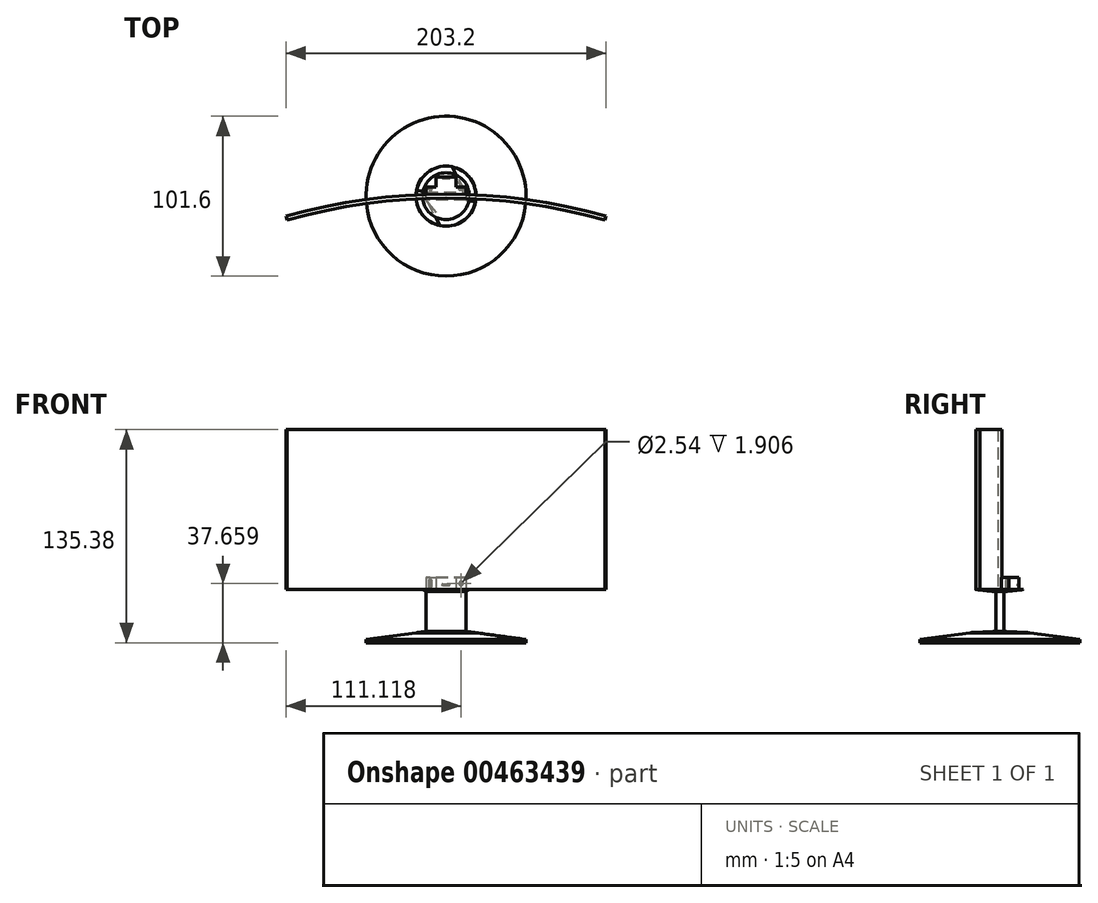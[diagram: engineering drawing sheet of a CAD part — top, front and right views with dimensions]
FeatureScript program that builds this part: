
annotation { "Feature Type Name" : "Feature", "Feature Type Description" : "" }
export const myFeature = defineFeature(function(context is Context, id is Id, definition is map)
    precondition{}
    {
        {
            var Q0;
            Q0=qCreatedBy(makeId("Top.planeOp"),FACE);
            var sketch = newSketch(context, id + "F0", { "sketchPlane" : qUnion([Q0])});
            skCircle(sketch, "E0", {"center": v(0, 0) * mm, "radius": 50.8 * mm});
            skSolve(sketch);
        }
        {
            var Q0;
            Q0=qCreatedBy(makeId("Top.planeOp"),FACE);
            cPlane(context, id + "F1", {"entities" : qUnion([Q0]), "cplaneType" : CPlaneType.OFFSET, "offset" : 4.32 * mm, "width" : 152.4 * mm, "height" : 152.4 * mm});
        }
        {
            var Q0;
            Q0=qCreatedBy(id+"F1.planeOp",FACE);
            var sketch = newSketch(context, id + "F2", { "sketchPlane" : qUnion([Q0])});
            skCircle(sketch, "E1", {"center": v(0, 0) * mm, "radius": 19.05 * mm});
            skSolve(sketch);
        }
        {
            var Q0;
            Q0=makeQuery(id+"F0.imprint","IMPRINT",FACE,{"disambiguationData":[TD([[makeQuery(id+"F0.imprint","IMPRINT",EDGE,{"derivedFrom":sQuery(id+"F0.wireOp",EDGE,"E0")}),1.0]])]});
            var Q1;
            Q1=makeQuery(id+"F2.imprint","IMPRINT",FACE,{"disambiguationData":[TD([[makeQuery(id+"F2.imprint","IMPRINT",EDGE,{"derivedFrom":sQuery(id+"F2.wireOp",EDGE,"E1")}),1.0]])]});
            loft(context, id + "F3", {"sheetProfilesArray" : [{ "sheetProfileEntities" : qUnion([Q0]) }, { "sheetProfileEntities" : qUnion([Q1]) }]});
        }
        {
            var Q0;
            Q0=qCreatedBy(makeId("Top.planeOp"),FACE);
            var sketch = newSketch(context, id + "F4", { "sketchPlane" : qUnion([Q0])});
            skCircle(sketch, "E2", {"center": v(0, 0) * mm, "radius": 50.8 * mm});
            skSolve(sketch);
        }
        {
            var Q0;
            Q0 = qSketchRegion(id + "F4", true);
            extrude(context, id + "F5", {"entities" : qUnion([Q0]), "operationType" : NewBodyOperationType.ADD, "depth" : -2.03 * mm});
        }
        {
            var Q0;
            Q0=qCreatedBy(makeId("Top.planeOp"),FACE);
            cPlane(context, id + "F6", {"entities" : qUnion([Q0]), "cplaneType" : CPlaneType.OFFSET, "offset" : 5.08 * mm, "width" : 152.4 * mm, "height" : 152.4 * mm});
        }
        {
            var Q0;
            Q0=qCreatedBy(id+"F6.planeOp",FACE);
            var sketch = newSketch(context, id + "F7", { "sketchPlane" : qUnion([Q0])});
            skLineSegment(sketch, "E3", {"start": v(-12.7, 2.54) * mm, "end": v(12.7, 2.54) * mm});
            skLineSegment(sketch, "E4", {"start": v(12.7, 2.54) * mm, "end": v(12.7, -2.54) * mm});
            skLineSegment(sketch, "E5", {"start": v(12.7, -2.54) * mm, "end": v(-12.7, -2.54) * mm});
            skPoint(sketch, "E6.end.orphan", {"position": v(-12.7, 0) * mm});
            skLineSegment(sketch, "E7", {"start": v(-12.7, -2.54) * mm, "end": v(-12.7, 2.54) * mm});
            skSolve(sketch);
        }
        {
            var Q0;
            Q0=makeQuery(id+"F7.imprint","IMPRINT",FACE,{"disambiguationData":[TD([[makeQuery(id+"F7.imprint","IMPRINT",EDGE,{"derivedFrom":sQuery(id+"F7.wireOp",EDGE,"E3")}),-1.0]])]});
            var Q1;
            Q1=makeQuery(id+"F3.opLoft","CAP_FACE",FACE,{"disambiguationData":[OSD([makeQuery(id+"F2.imprint","IMPRINT",FACE,{"disambiguationData":[TD([[makeQuery(id+"F2.imprint","IMPRINT",EDGE,{"derivedFrom":sQuery(id+"F2.wireOp",EDGE,"E1")}),1.0]])]})])],"isStart":true});
            loft(context, id + "F8", {"sheetProfilesArray" : [{ "sheetProfileEntities" : qUnion([Q0]) }, { "sheetProfileEntities" : qUnion([Q1]) }]});
        }
        {
            var Q0;
            Q0 = qSketchRegion(id + "F7", true);
            extrude(context, id + "F9", {"entities" : qUnion([Q0]), "operationType" : NewBodyOperationType.ADD, "depth" : 25.4 * mm});
        }
        {
            var Q0;
            Q0=qCreatedBy(makeId("Top.planeOp"),FACE);
            cPlane(context, id + "F10", {"entities" : qUnion([Q0]), "cplaneType" : CPlaneType.OFFSET, "offset" : 31.75 * mm, "width" : 152.4 * mm, "height" : 152.4 * mm});
        }
        {
            var Q0;
            Q0=qCreatedBy(id+"F10.planeOp",FACE);
            var sketch = newSketch(context, id + "F11", { "sketchPlane" : qUnion([Q0])});
            skCircle(sketch, "E8", {"center": v(0, 0) * mm, "radius": 14.86 * mm});
            skSolve(sketch);
        }
        {
            var Q1;
            Q1=makeQuery(id+"F9.opExtrude","CAP_FACE",FACE,{"disambiguationData":[OSD([sQuery(id+"F7.wireOp",EDGE,"E3"),sQuery(id+"F7.wireOp",EDGE,"E4"),sQuery(id+"F7.wireOp",EDGE,"E5"),sQuery(id+"F7.wireOp",EDGE,"E7")])],"isStart":false});
            var Q2;
            Q2=makeQuery(id+"F11.imprint","IMPRINT",FACE,{"disambiguationData":[TD([[makeQuery(id+"F11.imprint","IMPRINT",EDGE,{"derivedFrom":sQuery(id+"F11.wireOp",EDGE,"E8")}),1.0]])]});
            loft(context, id + "F12", {"operationType" : NewBodyOperationType.ADD, "sheetProfilesArray" : [{ "sheetProfileEntities" : qUnion([Q1]) }, { "sheetProfileEntities" : qUnion([Q2]) }]});
        }
        {
            var Q0;
            Q0=qCreatedBy(id+"F10.planeOp",FACE);
            var sketch = newSketch(context, id + "F13", { "sketchPlane" : qUnion([Q0])});
            skPoint(sketch, "E9.end.orphan", {"position": v(101.6, 0) * mm});
            skLineSegment(sketch, "E10", {"start": v(0, 0) * mm, "end": v(0, 1.27) * mm});
            skLineSegment(sketch, "E11", {"start": v(0, 1.27) * mm, "end": v(0, -1.27) * mm});
            skArc(sketch, "E12", {"start": v(101.6, -12.7) * mm, "mid": v(0, 1.27) * mm, "end": v(-101.6, -12.7) * mm});
            skLineSegment(sketch, "E13", {"start": v(-101.6, -12.7) * mm, "end": v(-100.93, -15.15) * mm});
            skLineSegment(sketch, "E14", {"start": v(101.6, -12.7) * mm, "end": v(100.93, -15.15) * mm});
            skArc(sketch, "E15", {"start": v(100.93, -15.15) * mm, "mid": v(0, -1.27) * mm, "end": v(-100.93, -15.15) * mm});
            skSolve(sketch);
        }
        {
            var Q0;
            Q0 = qSketchRegion(id + "F13", true);
            extrude(context, id + "F14", {"entities" : qUnion([Q0]), "operationType" : NewBodyOperationType.ADD, "depth" : 101.6 * mm});
        }
        {
            var Q0;
            Q0=qCreatedBy(id+"F10.planeOp",FACE);
            var sketch = newSketch(context, id + "F15", { "sketchPlane" : qUnion([Q0])});
            skLineSegment(sketch, "E16", {"start": v(0, 1.84) * mm, "end": v(-12.7, 1.84) * mm});
            skLineSegment(sketch, "E17", {"start": v(-12.7, 1.84) * mm, "end": v(-12.7, 5.9) * mm});
            skLineSegment(sketch, "E18", {"start": v(-12.7, 5.9) * mm, "end": v(-6.35, 5.9) * mm});
            skLineSegment(sketch, "E19", {"start": v(-6.35, 5.9) * mm, "end": v(-6.35, 12.24) * mm});
            skLineSegment(sketch, "E20", {"start": v(-6.35, 12.24) * mm, "end": v(6.35, 12.24) * mm});
            skLineSegment(sketch, "E21", {"start": v(6.35, 12.24) * mm, "end": v(6.35, 5.9) * mm});
            skLineSegment(sketch, "E22", {"start": v(6.35, 5.9) * mm, "end": v(12.7, 5.9) * mm});
            skLineSegment(sketch, "E23", {"start": v(12.7, 5.9) * mm, "end": v(12.7, 1.84) * mm});
            skLineSegment(sketch, "E24", {"start": v(12.7, 1.84) * mm, "end": v(0, 1.84) * mm});
            skSolve(sketch);
        }
        {
            var Q0;
            Q0 = qSketchRegion(id + "F15", true);
            extrude(context, id + "F16", {"entities" : qUnion([Q0]), "operationType" : NewBodyOperationType.ADD, "depth" : 7.62 * mm});
        }
        {
            var Q0;
            Q0=qCreatedBy(makeId("Front.planeOp"),FACE);
            cPlane(context, id + "F17", {"entities" : qUnion([Q0]), "cplaneType" : CPlaneType.OFFSET, "offset" : 1.85 * mm, "oppositeDirection" : true, "width" : 152.4 * mm, "height" : 152.4 * mm});
        }
        {
            var Q0;
            Q0=qCreatedBy(id+"F17.planeOp",FACE);
            var sketch = newSketch(context, id + "F18", { "sketchPlane" : qUnion([Q0])});
            skLineSegment(sketch, "E25", {"start": v(0, 31.75) * mm, "end": v(-12.7, 31.75) * mm});
            skLineSegment(sketch, "E26", {"start": v(-12.7, 31.75) * mm, "end": v(-12.7, 39.37) * mm});
            skLineSegment(sketch, "E27", {"start": v(-12.7, 39.37) * mm, "end": v(12.7, 39.37) * mm});
            skLineSegment(sketch, "E28", {"start": v(12.7, 39.37) * mm, "end": v(12.7, 31.75) * mm});
            skLineSegment(sketch, "E29", {"start": v(12.7, 31.75) * mm, "end": v(0, 31.75) * mm});
            skSolve(sketch);
        }
        {
            var Q0;
            Q0 = qSketchRegion(id + "F18", true);
            extrude(context, id + "F19", {"entities" : qUnion([Q0]), "operationType" : NewBodyOperationType.ADD, "depth" : 2.8 * mm});
        }
        {
            var Q0;
            Q0=qCreatedBy(makeId("Front.planeOp"),FACE);
            cPlane(context, id + "F20", {"entities" : qUnion([Q0]), "cplaneType" : CPlaneType.OFFSET, "offset" : 5.9 * mm, "oppositeDirection" : true, "width" : 152.4 * mm, "height" : 152.4 * mm});
        }
        {
            var Q0;
            Q0=qCreatedBy(id+"F20.planeOp",FACE);
            var sketch = newSketch(context, id + "F21", { "sketchPlane" : qUnion([Q0])});
            skPoint(sketch, "E30.start.orphan", {"position": v(0, 36.88) * mm});
            skLineSegment(sketch, "E31", {"start": v(-10.67, 38.08) * mm, "end": v(-10.67, 33) * mm});
            skLineSegment(sketch, "E32", {"start": v(-10.67, 33) * mm, "end": v(-9.52, 33) * mm});
            skLineSegment(sketch, "E33", {"start": v(-9.53, 33) * mm, "end": v(-9.33, 33.33) * mm});
            skPoint(sketch, "E34.start.orphan", {"position": v(0, 38.08) * mm});
            skLineSegment(sketch, "E35", {"start": v(-10.67, 38.08) * mm, "end": v(-9.53, 38.08) * mm});
            skLineSegment(sketch, "E36", {"start": v(-9.52, 38.08) * mm, "end": v(-9.33, 37.75) * mm});
            skLineSegment(sketch, "E37", {"start": v(-9.33, 37.75) * mm, "end": v(-9.04, 37.5) * mm});
            skLineSegment(sketch, "E38", {"start": v(-9.33, 33.33) * mm, "end": v(-9.04, 33.57) * mm});
            skLineSegment(sketch, "E39", {"start": v(-9.04, 33.57) * mm, "end": v(-9.04, 37.5) * mm});
            skCircle(sketch, "E40", {"center": v(9.52, 35.63) * mm, "radius": 1.27 * mm});
            skPoint(sketch, "E41.start.orphan", {"position": v(0, 35.63) * mm});
            skCircle(sketch, "E42", {"center": v(9.52, 35.63) * mm, "radius": 0.64 * mm});
            skLineSegment(sketch, "E43", {"start": v(-9.75, 37.5) * mm, "end": v(-9.75, 33.57) * mm});
            skLineSegment(sketch, "E44", {"start": v(-9.75, 33.57) * mm, "end": v(-10, 33.57) * mm});
            skLineSegment(sketch, "E45", {"start": v(-10, 33.57) * mm, "end": v(-10, 37.5) * mm});
            skLineSegment(sketch, "E46", {"start": v(-10, 37.5) * mm, "end": v(-9.75, 37.5) * mm});
            skSolve(sketch);
        }
        {
            var Q0;
            Q0 = qSketchRegion(id + "F21", true);
            var Q1;
            Q1=sQuery(id+"F21.wireOp",EDGE,"E40");
            extrude(context, id + "F22", {"entities" : qUnion([Q0]), "operationType" : NewBodyOperationType.REMOVE, "surfaceEntities" : qUnion([Q1]), "depth" : 1.9 * mm});
        }
        {
            var Q0;
            Q0=qCreatedBy(makeId("Front.planeOp"),FACE);
            cPlane(context, id + "F23", {"entities" : qUnion([Q0]), "cplaneType" : CPlaneType.OFFSET, "offset" : 12.24 * mm, "oppositeDirection" : true, "width" : 152.4 * mm, "height" : 152.4 * mm});
        }
        {
            var Q0;
            Q0=qCreatedBy(id+"F23.planeOp",FACE);
            var sketch = newSketch(context, id + "F24", { "sketchPlane" : qUnion([Q0])});
            skLineSegment(sketch, "E47", {"start": v(0, 34.14) * mm, "end": v(-1.9, 34.14) * mm});
            skLineSegment(sketch, "E48", {"start": v(-1.9, 34.14) * mm, "end": v(1.9, 34.14) * mm});
            skLineSegment(sketch, "E49", {"start": v(1.9, 34.14) * mm, "end": v(2.49, 34.98) * mm});
            skLineSegment(sketch, "E50", {"start": v(-1.9, 34.14) * mm, "end": v(-2.49, 34.98) * mm});
            skLineSegment(sketch, "E51", {"start": v(2.49, 34.98) * mm, "end": v(2.49, 34.98) * mm});
            skLineSegment(sketch, "E52", {"start": v(2.1, 35.36) * mm, "end": v(-2.1, 35.36) * mm});
            skLineSegment(sketch, "E53", {"start": v(-2.49, 34.98) * mm, "end": v(-2.49, 34.98) * mm});
            skPoint(sketch, "E54.visualSharp", {"position": v(-2.49, 35.36) * mm});
            skArc(sketch, "E54.filletArc", {"start": v(-2.1, 35.36) * mm, "mid": v(-2.38, 35.25) * mm, "end": v(-2.49, 34.98) * mm});
            skPoint(sketch, "E55.visualSharp", {"position": v(2.49, 35.36) * mm});
            skArc(sketch, "E55.filletArc", {"start": v(2.49, 34.98) * mm, "mid": v(2.38, 35.25) * mm, "end": v(2.1, 35.36) * mm});
            skCircle(sketch, "E56", {"center": v(1.87, 34.98) * mm, "radius": 0.13 * mm});
            skCircle(sketch, "E57", {"center": v(1.69, 34.54) * mm, "radius": 0.13 * mm});
            skCircle(sketch, "E58", {"center": v(1.46, 34.98) * mm, "radius": 0.13 * mm});
            skCircle(sketch, "E59", {"center": v(1.09, 34.54) * mm, "radius": 0.13 * mm});
            skCircle(sketch, "E60", {"center": v(1.09, 34.98) * mm, "radius": 0.13 * mm});
            skCircle(sketch, "E61", {"center": v(0.72, 34.98) * mm, "radius": 0.13 * mm});
            skCircle(sketch, "E62", {"center": v(0.7, 34.54) * mm, "radius": 0.13 * mm});
            skCircle(sketch, "E63", {"center": v(0.28, 34.98) * mm, "radius": 0.13 * mm});
            skCircle(sketch, "E64", {"center": v(0.25, 34.54) * mm, "radius": 0.13 * mm});
            skCircle(sketch, "E65", {"center": v(-0.18, 34.54) * mm, "radius": 0.13 * mm});
            skCircle(sketch, "E66", {"center": v(-0.2, 34.98) * mm, "radius": 0.13 * mm});
            skCircle(sketch, "E67", {"center": v(-0.65, 34.98) * mm, "radius": 0.13 * mm});
            skCircle(sketch, "E68", {"center": v(-0.72, 34.54) * mm, "radius": 0.13 * mm});
            skCircle(sketch, "E69", {"center": v(-1.16, 34.54) * mm, "radius": 0.13 * mm});
            skCircle(sketch, "E70", {"center": v(-1.17, 34.98) * mm, "radius": 0.13 * mm});
            skCircle(sketch, "E71", {"center": v(-1.65, 34.98) * mm, "radius": 0.13 * mm});
            skCircle(sketch, "E72", {"center": v(-1.7, 34.54) * mm, "radius": 0.13 * mm});
            skCircle(sketch, "E73", {"center": v(-2.1, 34.98) * mm, "radius": 0.13 * mm});
            skSolve(sketch);
        }
        {
            var Q0;
            Q0 = qSketchRegion(id + "F24", true);
            extrude(context, id + "F25", {"entities" : qUnion([Q0]), "operationType" : NewBodyOperationType.REMOVE, "depth" : 1.02 * mm});
        }
    });
